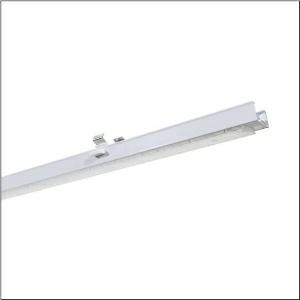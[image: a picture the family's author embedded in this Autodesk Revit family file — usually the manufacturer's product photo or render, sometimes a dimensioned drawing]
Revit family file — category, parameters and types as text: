
# Revit family: trunking_flex_31_51re11mb48b
name_source: partatom
category: Lighting Fixtures
units: mm (PartAtom-declared; Revit-internal decimal feet)

## family parameters
Cut with Voids When Loaded = No
Host = Face
Light Source = No
Part Type = Normal
Room Calculation Point = No
Round Connector Dimension = Use Diameter
Shared = No

## types (1)
- --- (1 x LED, 8000 lm, 50 W, 4000K)
    Apparent Load = 50 VA
    CIE Flux Codes = 83 93 98 100 100
    Color Rendering = 80
    Color Temperature = 4000K
    Default Elevation = 1800 mm
    Description = Trunking Flex 31, luminaire insert, of extruded aluminium section, coated, traffic white (RAL 9016), length: 1.472mm, width: 91mm, height: 53mm, LED rated luminous flux: 8.000lm, light colour: 840, control gear: ON/OFF Multilumen, with system connector: socket, mains connection: 220..240V, AC, 50/60Hz, rated input power: 50W, luminous flux adjustable on luminaire in four steps (4130/5610/6850/8000lm), connected load according to luminous flux setting (25/34/42/50W), primary light control with lens, of plastic, primary optical cover: cover, of PMMA, light emission: direct distribution, protection rating (complete): IP20, insulation class (complete): insulation class I (protective earthing), certification: CE, UKCA, impact resistance: IK02, permissible ambient temperature for indoor applications: -20..+40°C, packaging unit: 1 piece
    Height = 58 mm
    Lamp = 1 x LED
    Lamp Light Flux = 8000 lm
    Lamp Power = 50 W
    Lamp count = 1
    Length = 1472 mm
    Luminous efficacy = 160 lm/W
    Manufacturer = Siteco
    ModVariant = No
    Model = 51RE11MB48B
    Mounting Place = Ceiling
    Mounting Type = Pendant
    Number of Poles = 1
    OnlyDefault = Yes
    Power Factor = 1
    Product Name = Trunking Flex 31
    Product group = luminaire insert
    ProductGroupID = 902
    Protection Class = Protection class I
    Protection Degree = IP 20
    RLX_Detail_Level = 1
    RLX_Emergency_Light_Flux = 0 lm
    RLX_Emergency_Type = 0
    RLX_Emergency_Type_DB = No
    RlxData = <blob elided: 20209 chars, md5=fbec49a3>
    Socket = socket
    Standby Power = 0 W
    System Light Flux = 8000 lm
    System Power = 50 W
    Type Comments = factory setting: luminous flux: 100 % | (ON | ON) | 300 mA
    Type Image = l_1266702.jpg
    URL = http://relux.com
    VarID = @adj_059274
    Voltage = 0 V
    Weight = 0.00 kg
    Width = 65 mm

## geometry (parser evidence)
native form markers: Blend x4, Sweep x10
no freeform markers — native parametric forms only
